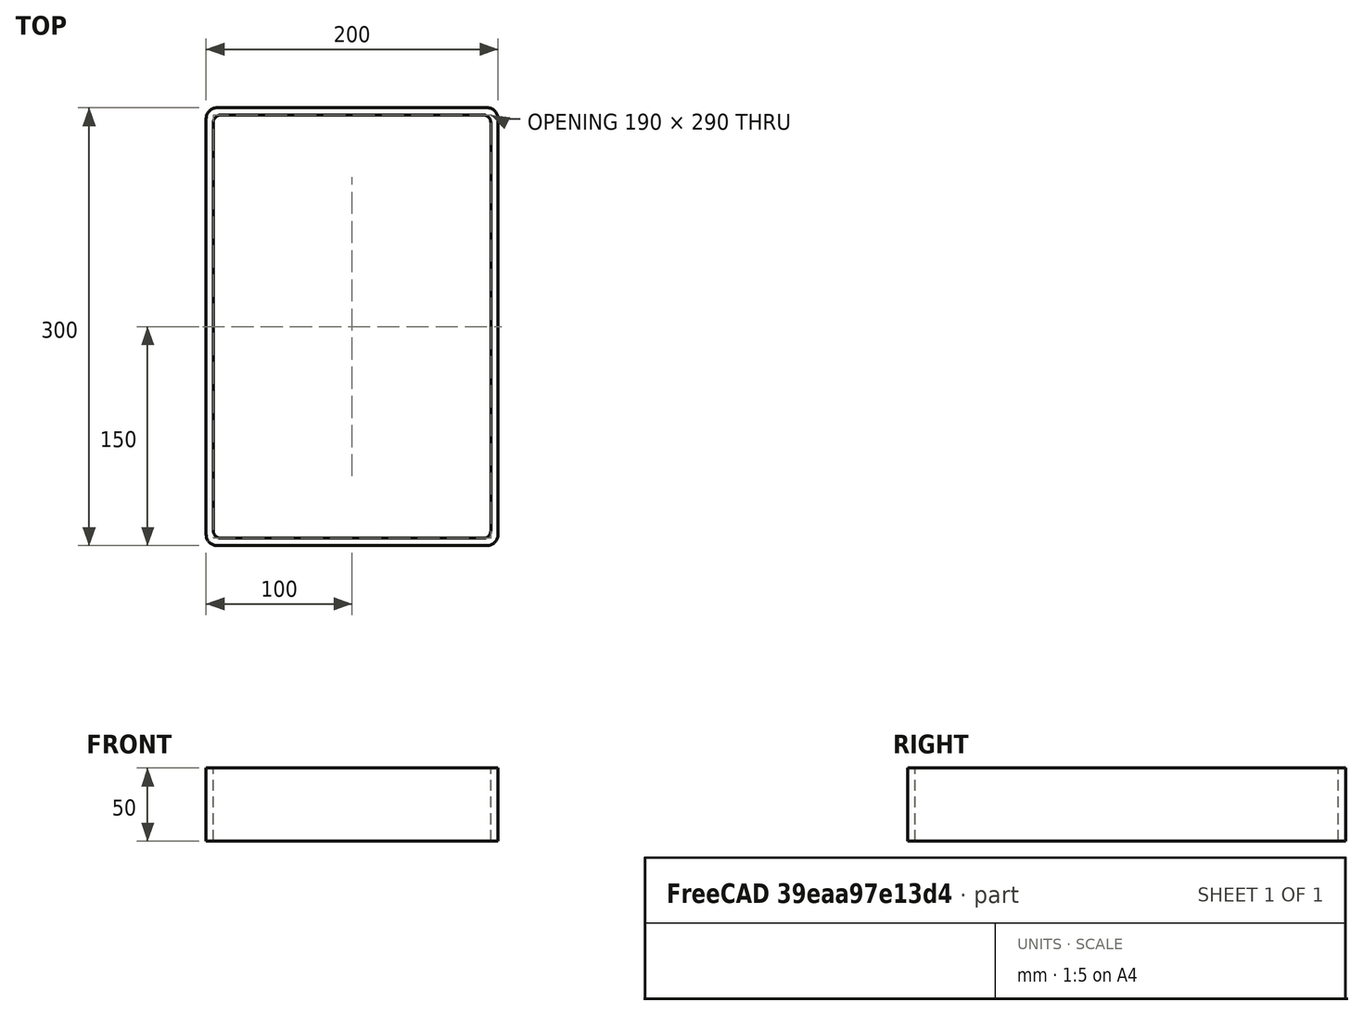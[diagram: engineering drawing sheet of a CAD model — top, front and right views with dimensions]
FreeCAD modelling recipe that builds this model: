
FCSTD DOCUMENT  (FreeCAD 0.15R4671 (Git))
Label: Rectangular hollow section 300x200x5 EN10219 S235JRH
License: All rights reserved
LicenseURL: http://en.wikipedia.org/wiki/All_rights_reserved
objects: Sketcher::SketchObject×1, Part::Extrusion×1
note: 2 computed .brp shape members not serialized (recipe doc carries the construction recipe); baked Part::Feature solids carry a one-line shape summary decoded from their .brp

FEATURE [Sketcher::SketchObject] Sketch
  sketch-geometry (16):
    g0: LineSegment StartX=-90 StartY=145 StartZ=0 EndX=90 EndY=145 EndZ=0
    g1: LineSegment StartX=95 StartY=140 StartZ=0 EndX=95 EndY=-140 EndZ=0
    g2: LineSegment StartX=90 StartY=-145 StartZ=0 EndX=-90 EndY=-145 EndZ=0
    g3: LineSegment StartX=-95 StartY=-140 StartZ=0 EndX=-95 EndY=140 EndZ=0
    g4: LineSegment StartX=-92.5 StartY=150 StartZ=0 EndX=92.5 EndY=150 EndZ=0
    g5: LineSegment StartX=100 StartY=142.5 StartZ=0 EndX=100 EndY=-142.5 EndZ=0
    g6: LineSegment StartX=92.5 StartY=-150 StartZ=0 EndX=-92.5 EndY=-150 EndZ=0
    g7: LineSegment StartX=-100 StartY=-142.5 StartZ=0 EndX=-100 EndY=142.5 EndZ=0
    g8: ArcOfCircle CenterX=-90 CenterY=140 CenterZ=0 NormalX=0 NormalY=0 NormalZ=1 Radius=5 StartAngle=1.5708 EndAngle=3.14159
    g9: ArcOfCircle CenterX=90 CenterY=140 CenterZ=0 NormalX=0 NormalY=0 NormalZ=1 Radius=5 StartAngle=0 EndAngle=1.5708
    g10: ArcOfCircle CenterX=90 CenterY=-140 CenterZ=0 NormalX=0 NormalY=0 NormalZ=1 Radius=5 StartAngle=4.71239 EndAngle=6.28319
    g11: ArcOfCircle CenterX=-90 CenterY=-140 CenterZ=0 NormalX=0 NormalY=0 NormalZ=1 Radius=5 StartAngle=3.14159 EndAngle=4.71239
    g12: ArcOfCircle CenterX=92.5 CenterY=142.5 CenterZ=0 NormalX=0 NormalY=0 NormalZ=1 Radius=7.5 StartAngle=0 EndAngle=1.5708
    g13: ArcOfCircle CenterX=92.5 CenterY=-142.5 CenterZ=0 NormalX=0 NormalY=0 NormalZ=1 Radius=7.5 StartAngle=4.71239 EndAngle=6.28319
    g14: ArcOfCircle CenterX=-92.5 CenterY=-142.5 CenterZ=0 NormalX=0 NormalY=0 NormalZ=1 Radius=7.5 StartAngle=3.14159 EndAngle=4.71239
    g15: ArcOfCircle CenterX=-92.5 CenterY=142.5 CenterZ=0 NormalX=0 NormalY=0 NormalZ=1 Radius=7.5 StartAngle=1.5708 EndAngle=3.14159
  constraints (36):
    c: Horizontal(g2)
    c: Vertical(g3)
    c: Horizontal(g6)
    c: Vertical(g7)
    c: Tangent(g3,g8) = 1.5708
    c: Tangent(g0,g8) = 1.5708
    c: Tangent(g0,g9) = 1.5708
    c: Tangent(g1,g9) = 1.5708
    c: Tangent(g1,g10) = 1.5708
    c: Tangent(g2,g10) = 1.5708
    c: Tangent(g2,g11) = 1.5708
    c: Tangent(g3,g11) = 1.5708
    c: Tangent(g4,g12) = 1.5708
    c: Tangent(g5,g12) = 1.5708
    c: Tangent(g5,g13) = 1.5708
    c: Tangent(g6,g13) = 1.5708
    c: Tangent(g6,g14) = 1.5708
    c: Tangent(g7,g14) = 1.5708
    c: Tangent(g7,g15) = 1.5708
    c: Tangent(g4,g15) = 1.5708
    c: Equal(g9,g8)
    c: Equal(g9,g11)
    c: Equal(g9,g10)
    c: Equal(g12,g15)
    c: Equal(g12,g14)
    c: Equal(g12,g13)
    c: Symmetric(g4,g6,g-1)
    c: Symmetric(g7,g5,g-2)
    c: DistanceY(g4,g6) = -300
    c: DistanceX(g7,g5) = 200
    c: Symmetric(g3,g1,g-2)
    c: Symmetric(g0,g2,g-1)
    c: DistanceY(g0,g4) = 5
    c: DistanceX(g5,g1) = -5
    c: Radius(g9) = 5
    c: Radius(g12) = 7.5
FEATURE [Part::Extrusion] Extrude  label="Rectangular hollow section 300x200x5 EN10219 S235JRH"
  Base = -> Sketch
  Dir = (0,0,50)
  Solid = true
